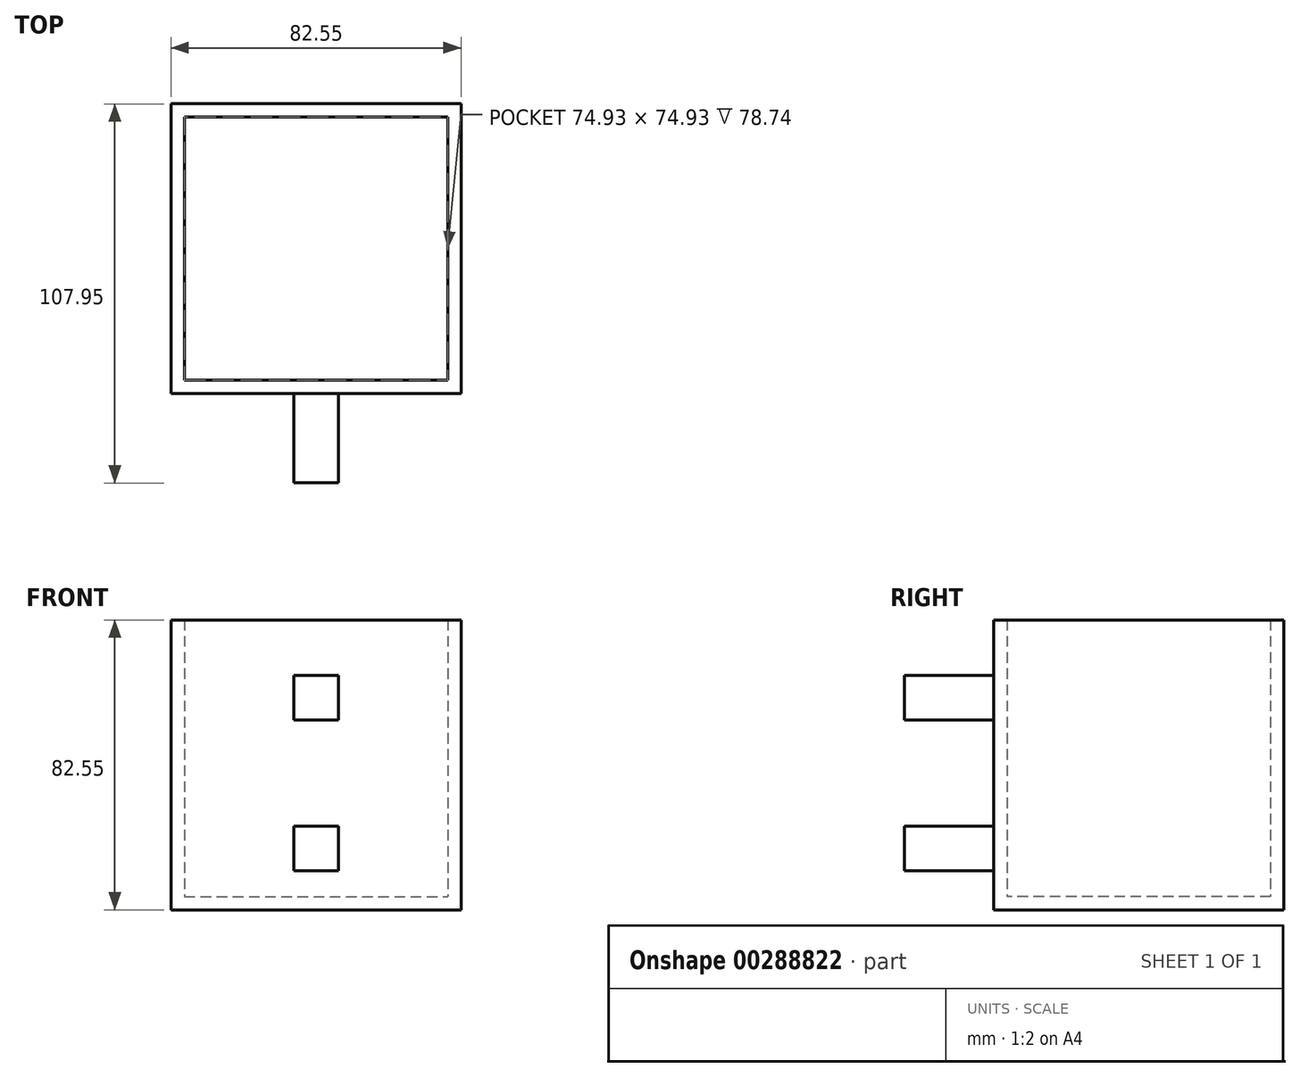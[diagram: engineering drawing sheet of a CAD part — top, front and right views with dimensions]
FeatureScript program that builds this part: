
annotation { "Feature Type Name" : "Feature", "Feature Type Description" : "" }
export const myFeature = defineFeature(function(context is Context, id is Id, definition is map)
    precondition{}
    {
        {
            var Q0;
            Q0=qCreatedBy(makeId("Top.planeOp"),FACE);
            var sketch = newSketch(context, id + "F0", { "sketchPlane" : qUnion([Q0])});
            skLineSegment(sketch, "E0.bottom", {"start": v(25.02, 44.4) * mm, "end": v(99.95, 44.4) * mm});
            skLineSegment(sketch, "E0.top", {"start": v(25.02, -30.54) * mm, "end": v(99.95, -30.54) * mm});
            skLineSegment(sketch, "E0.left", {"start": v(25.02, 44.4) * mm, "end": v(25.02, -30.54) * mm});
            skLineSegment(sketch, "E0.right", {"start": v(99.95, 44.4) * mm, "end": v(99.95, -30.54) * mm});
            skLineSegment(sketch, "E1.0", {"start": v(21.2, 48.2) * mm, "end": v(21.2, -34.35) * mm});
            skLineSegment(sketch, "E1.1", {"start": v(21.2, 48.2) * mm, "end": v(103.76, 48.2) * mm});
            skLineSegment(sketch, "E1.2", {"start": v(103.76, 48.2) * mm, "end": v(103.76, -34.35) * mm});
            skLineSegment(sketch, "E1.3", {"start": v(21.2, -34.35) * mm, "end": v(103.76, -34.35) * mm});
            skSolve(sketch);
        }
        {
            var Q0;
            Q0=makeQuery(id+"F0.imprint","IMPRINT",FACE,{"disambiguationData":[TD([[makeQuery(id+"F0.imprint","IMPRINT",EDGE,{"derivedFrom":sQuery(id+"F0.wireOp",EDGE,"E0.bottom")}),1.0]])]});
            extrude(context, id + "F1", {"entities" : qUnion([Q0]), "depth" : 82.55 * mm});
        }
        {
            var Q0;
            Q0=makeQuery(id+"F0.imprint","IMPRINT",FACE,{"disambiguationData":[TD([[makeQuery(id+"F0.imprint","IMPRINT",EDGE,{"derivedFrom":sQuery(id+"F0.wireOp",EDGE,"E0.bottom")}),-1.0]])]});
            extrude(context, id + "F2", {"entities" : qUnion([Q0]), "operationType" : NewBodyOperationType.ADD, "depth" : 3.8 * mm});
        }
        {
            var Q0;
            Q0=makeQuery(id+"F1.opExtrude","SWEPT_FACE",FACE,{"disambiguationData":[OSD([sQuery(id+"F0.wireOp",EDGE,"E1.3")])]});
            var sketch = newSketch(context, id + "F3", { "sketchPlane" : qUnion([Q0])});
            skPoint(sketch, "E2.endSnap0", {"position": v(103.76, 41.28) * mm});
            skLineSegment(sketch, "E3.bottom", {"start": v(48.2, 47.63) * mm, "end": v(35.5, 47.63) * mm});
            skLineSegment(sketch, "E3.top", {"start": v(48.2, 34.93) * mm, "end": v(35.5, 34.93) * mm});
            skLineSegment(sketch, "E3.left", {"start": v(48.2, 47.63) * mm, "end": v(48.2, 34.93) * mm});
            skLineSegment(sketch, "E3.right", {"start": v(35.5, 47.63) * mm, "end": v(35.5, 34.93) * mm});
            skPoint(sketch, "E3.middle", {"position": v(41.84, 41.28) * mm});
            skLineSegment(sketch, "E4.bottom", {"start": v(89.47, 34.93) * mm, "end": v(76.77, 34.93) * mm});
            skLineSegment(sketch, "E4.top", {"start": v(89.47, 47.63) * mm, "end": v(76.77, 47.63) * mm});
            skLineSegment(sketch, "E4.left", {"start": v(89.47, 34.93) * mm, "end": v(89.47, 47.63) * mm});
            skLineSegment(sketch, "E4.right", {"start": v(76.77, 34.93) * mm, "end": v(76.77, 47.63) * mm});
            skPoint(sketch, "E4.middle", {"position": v(83.12, 41.28) * mm});
            skLineSegment(sketch, "E5", {"start": v(21.2, 41.28) * mm, "end": v(103.76, 41.28) * mm, "construction": true});
            skLineSegment(sketch, "E6.bottom", {"start": v(68.83, 54.02) * mm, "end": v(56.13, 54.02) * mm});
            skLineSegment(sketch, "E6.top", {"start": v(68.83, 66.72) * mm, "end": v(56.13, 66.72) * mm});
            skLineSegment(sketch, "E6.left", {"start": v(68.83, 54.02) * mm, "end": v(68.83, 66.72) * mm});
            skLineSegment(sketch, "E6.right", {"start": v(56.13, 54.02) * mm, "end": v(56.13, 66.72) * mm});
            skPoint(sketch, "E6.middle", {"position": v(62.48, 60.37) * mm});
            skLineSegment(sketch, "E7.bottom", {"start": v(68.83, 11.13) * mm, "end": v(56.13, 11.13) * mm});
            skLineSegment(sketch, "E7.top", {"start": v(68.83, 23.83) * mm, "end": v(56.13, 23.83) * mm});
            skLineSegment(sketch, "E7.left", {"start": v(68.83, 11.13) * mm, "end": v(68.83, 23.83) * mm});
            skLineSegment(sketch, "E7.right", {"start": v(56.13, 11.13) * mm, "end": v(56.13, 23.83) * mm});
            skPoint(sketch, "E7.middle", {"position": v(62.48, 17.48) * mm});
            skLineSegment(sketch, "E8", {"start": v(62.48, 82.55) * mm, "end": v(62.48, 0) * mm, "construction": true});
            skSolve(sketch);
        }
        {
            var Q0;
            Q0=makeQuery(id+"F3.imprint","IMPRINT",FACE,{"disambiguationData":[TD([[makeQuery(id+"F3.imprint","IMPRINT",EDGE,{"derivedFrom":sQuery(id+"F3.wireOp",EDGE,"E6.bottom")}),-1.0]])]});
            var Q1;
            Q1=makeQuery(id+"F3.imprint","IMPRINT",FACE,{"disambiguationData":[TD([[makeQuery(id+"F3.imprint","IMPRINT",EDGE,{"derivedFrom":sQuery(id+"F3.wireOp",EDGE,"E7.bottom")}),-1.0]])]});
            extrude(context, id + "F4", {"entities" : qUnion([Q0, Q1]), "operationType" : NewBodyOperationType.ADD, "depth" : 25.4 * mm});
        }
    });
